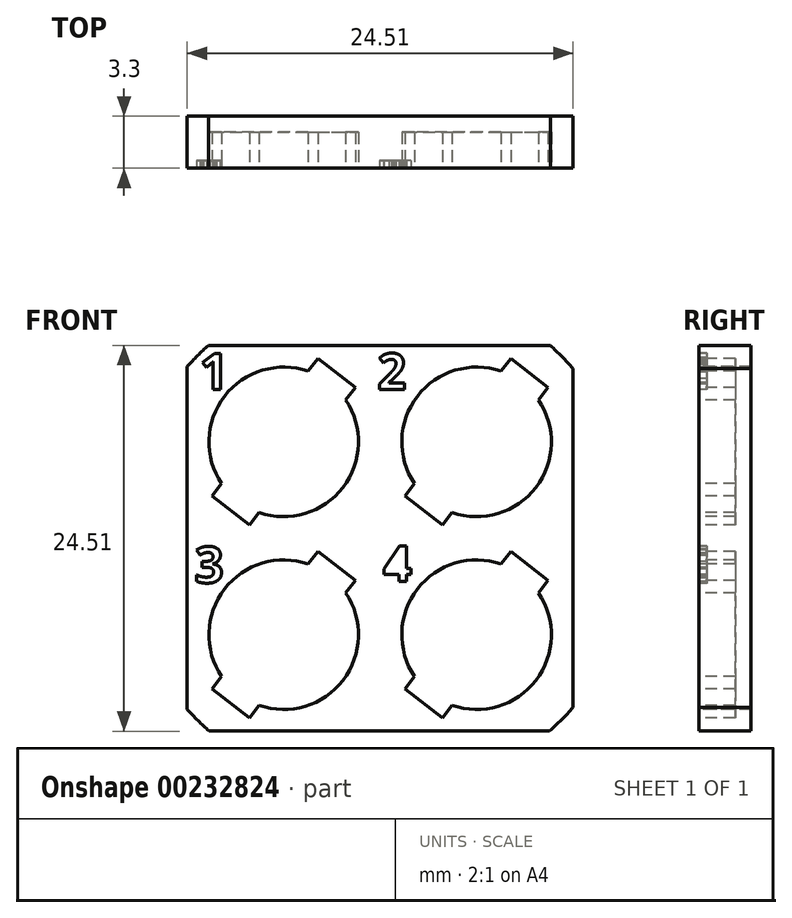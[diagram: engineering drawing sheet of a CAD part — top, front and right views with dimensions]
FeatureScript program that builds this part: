
annotation { "Feature Type Name" : "Feature", "Feature Type Description" : "" }
export const myFeature = defineFeature(function(context is Context, id is Id, definition is map)
    precondition{}
    {
        {
            var Q0;
            Q0=qCreatedBy(makeId("Front.planeOp"),FACE);
            var sketch = newSketch(context, id + "F0", { "sketchPlane" : qUnion([Q0])});
            skLineSegment(sketch, "E0.bottom", {"start": v(6.13, -6.13) * mm, "end": v(-6.12, -6.13) * mm});
            skLineSegment(sketch, "E0.top", {"start": v(6.12, 6.13) * mm, "end": v(-6.13, 6.12) * mm});
            skLineSegment(sketch, "E0.left", {"start": v(6.13, -6.13) * mm, "end": v(6.12, 6.12) * mm});
            skLineSegment(sketch, "E0.right", {"start": v(-6.12, -6.13) * mm, "end": v(-6.13, 6.12) * mm});
            skPoint(sketch, "E0.middle", {"position": v(0, 0) * mm});
            skSolve(sketch);
        }
        {
            var Q0;
            Q0=qSketchRegion(id+"F0",true);
            extrude(context, id + "F1", {"entities" : qUnion([Q0]), "oppositeDirection" : true, "depth" : 3.3 * mm, "offsetDistance" : 25 * mm});
        }
        {
            var Q0;
            Q0=qCreatedBy(makeId("Front.planeOp"),FACE);
            var sketch = newSketch(context, id + "F2", { "sketchPlane" : qUnion([Q0])});
            skCircle(sketch, "E1", {"center": v(0, 0) * mm, "radius": 4.75 * mm});
            skLineSegment(sketch, "E2", {"start": v(1.56, 4.49) * mm, "end": v(2.17, 5.28) * mm});
            skLineSegment(sketch, "E3", {"start": v(2.17, 5.28) * mm, "end": v(4.55, 3.45) * mm});
            skLineSegment(sketch, "E4", {"start": v(4.55, 3.45) * mm, "end": v(3.94, 2.66) * mm});
            skLineSegment(sketch, "E5", {"start": v(-3.94, -2.66) * mm, "end": v(-4.55, -3.45) * mm});
            skLineSegment(sketch, "E6", {"start": v(-4.55, -3.45) * mm, "end": v(-2.17, -5.28) * mm});
            skLineSegment(sketch, "E7", {"start": v(-2.17, -5.28) * mm, "end": v(-1.56, -4.49) * mm});
            skSolve(sketch);
        }
        {
            var Q0;
            {var subQ0=sQuery(id+"F2.wireOp",EDGE,"E5");Q0=makeQuery(id+"F2.imprint","IMPRINT",FACE,{"disambiguationData":[TD([[makeQuery(id+"F2.imprint","IMPRINT",EDGE,{"derivedFrom":subQ0}),1.0]])]});}
            var Q1;
            {var subQ0=sQuery(id+"F2.wireOp",EDGE,"E2");Q1=makeQuery(id+"F2.imprint","IMPRINT",FACE,{"disambiguationData":[TD([[makeQuery(id+"F2.imprint","IMPRINT",EDGE,{"derivedFrom":subQ0}),-1.0]])]});}
            var Q2;
            {var subQ0=sQuery(id+"F2.wireOp",EDGE,"E1");var subQ1=makeQuery(id+"F2.imprint","INTERSECT",VERTEX,{"derivedFrom":[subQ0,sQuery(id+"F2.wireOp",EDGE,"E2")]});Q2=makeQuery(id+"F2.imprint","IMPRINT",FACE,{"disambiguationData":[TD([[makeQuery(id+"F2.imprint","IMPRINT",EDGE,{"disambiguationData":[TD([[subQ1,1.0]])],"derivedFrom":subQ0}),1.0]])]});}
            extrude(context, id + "F3", {"entities" : qUnion([Q0, Q1, Q2]), "operationType" : NewBodyOperationType.REMOVE, "oppositeDirection" : true, "depth" : 2.3 * mm, "offsetDistance" : 25 * mm});
        }
        {
            var Q0;
            Q0=makeQuery(id+"F1.opExtrude","SWEPT_BODY",BODY,{"disambiguationData":[OSD([sQuery(id+"F0.wireOp",EDGE,"E0.bottom"),sQuery(id+"F0.wireOp",EDGE,"E0.top"),sQuery(id+"F0.wireOp",EDGE,"E0.left"),sQuery(id+"F0.wireOp",EDGE,"E0.right")])]});
            transform(context, id + "F4", {"entities" : qUnion([Q0]), "transformType" : TransformType.TRANSLATION_3D, "dx" : -12.25 * mm, "dy" : 0 * mm, "dz" : 0 * mm, "makeCopy" : true});
        }
        {
            var Q0;
            Q0=makeQuery(id+"F1.opExtrude","SWEPT_BODY",BODY,{"disambiguationData":[OSD([sQuery(id+"F0.wireOp",EDGE,"E0.bottom"),sQuery(id+"F0.wireOp",EDGE,"E0.top"),sQuery(id+"F0.wireOp",EDGE,"E0.left"),sQuery(id+"F0.wireOp",EDGE,"E0.right")])]});
            transform(context, id + "F5", {"entities" : qUnion([Q0]), "transformType" : TransformType.TRANSLATION_3D, "dx" : 0 * mm, "dy" : 0 * mm, "dz" : 12.25 * mm, "makeCopy" : true});
        }
        {
            var Q0;
            Q0=makeQuery(id+"F1.opExtrude","SWEPT_BODY",BODY,{"disambiguationData":[OSD([sQuery(id+"F0.wireOp",EDGE,"E0.bottom"),sQuery(id+"F0.wireOp",EDGE,"E0.top"),sQuery(id+"F0.wireOp",EDGE,"E0.left"),sQuery(id+"F0.wireOp",EDGE,"E0.right")])]});
            transform(context, id + "F6", {"entities" : qUnion([Q0]), "transformType" : TransformType.TRANSLATION_3D, "dx" : -12.25 * mm, "dy" : 0 * mm, "dz" : 12.25 * mm, "makeCopy" : true});
        }
        {
            var Q0;
            Q0=makeQuery(id+"F1.opExtrude","SWEPT_BODY",BODY,{"disambiguationData":[OSD([sQuery(id+"F0.wireOp",EDGE,"E0.bottom"),sQuery(id+"F0.wireOp",EDGE,"E0.top"),sQuery(id+"F0.wireOp",EDGE,"E0.left"),sQuery(id+"F0.wireOp",EDGE,"E0.right")])]});
            var Q1;
            Q1=makeQuery(id+"F4.opPattern","COPY",BODY,{"derivedFrom":makeQuery(id+"F1.opExtrude","SWEPT_BODY",BODY,{"disambiguationData":[OSD([sQuery(id+"F0.wireOp",EDGE,"E0.bottom"),sQuery(id+"F0.wireOp",EDGE,"E0.top"),sQuery(id+"F0.wireOp",EDGE,"E0.left"),sQuery(id+"F0.wireOp",EDGE,"E0.right")])]}),"instanceName":"1"});
            var Q2;
            Q2=makeQuery(id+"F5.opPattern","COPY",BODY,{"derivedFrom":makeQuery(id+"F1.opExtrude","SWEPT_BODY",BODY,{"disambiguationData":[OSD([sQuery(id+"F0.wireOp",EDGE,"E0.bottom"),sQuery(id+"F0.wireOp",EDGE,"E0.top"),sQuery(id+"F0.wireOp",EDGE,"E0.left"),sQuery(id+"F0.wireOp",EDGE,"E0.right")])]}),"instanceName":"1"});
            var Q3;
            Q3=makeQuery(id+"F6.opPattern","COPY",BODY,{"derivedFrom":makeQuery(id+"F1.opExtrude","SWEPT_BODY",BODY,{"disambiguationData":[OSD([sQuery(id+"F0.wireOp",EDGE,"E0.bottom"),sQuery(id+"F0.wireOp",EDGE,"E0.top"),sQuery(id+"F0.wireOp",EDGE,"E0.left"),sQuery(id+"F0.wireOp",EDGE,"E0.right")])]}),"instanceName":"1"});
            booleanBodies(context, id + "F7", {"operationType" : BooleanOperationType.UNION, "tools" : qUnion([Q0, Q1, Q2, Q3])});
        }
        {
            var Q0;
            {var subQ0=makeQuery(id+"F1.opExtrude","CAP_FACE",FACE,{"disambiguationData":[OSD([sQuery(id+"F0.wireOp",EDGE,"E0.bottom"),sQuery(id+"F0.wireOp",EDGE,"E0.top"),sQuery(id+"F0.wireOp",EDGE,"E0.left"),sQuery(id+"F0.wireOp",EDGE,"E0.right")])],"isStart":true});Q0=makeQuery(id+"F7.opBoolean","MERGE",FACE,{"derivedFrom":[subQ0,makeQuery(id+"F4.opPattern","COPY",FACE,{"derivedFrom":subQ0,"instanceName":"1"}),makeQuery(id+"F5.opPattern","COPY",FACE,{"derivedFrom":subQ0,"instanceName":"1"}),makeQuery(id+"F6.opPattern","COPY",FACE,{"derivedFrom":subQ0,"instanceName":"1"})]});}
            var sketch = newSketch(context, id + "F8", { "sketchPlane" : qUnion([Q0])});
            skText(sketch, "E8", { "text": "1", "fontName": "OpenSans-Bold.ttf"});
            skPoint(sketch, "E8.secondSnap0", {"position": v(-7.61, 15.58) * mm});
            skText(sketch, "E9", { "text": "2", "fontName": "OpenSans-Bold.ttf"});
            skPoint(sketch, "E9.secondSnap0", {"position": v(-3.98, 15.58) * mm});
            skText(sketch, "E10", { "text": "3", "fontName": "OpenSans-Bold.ttf"});
            skPoint(sketch, "E10.secondSnap0", {"position": v(-16.02, 2.9) * mm});
            skText(sketch, "E11", { "text": "4", "fontName": "OpenSans-Bold.ttf"});
            const initialGuessF8  = {"E8": [-0.01758, 0.01558, 1, 0, 0.0023], "E9": [-0.0063, 0.01558, 1, 0, 0.0023], "E10": [-0.0179, 0.0033, 1, 0, 0.0023], "E11": [-0.00595, 0.00337, 1, 0, 0.0023]};
            skSetInitialGuess(sketch, initialGuessF8);
            skSolve(sketch);
        }
        {
            var Q0;
            Q0=qSketchRegion(id+"F8",true);
            extrude(context, id + "F9", {"entities" : qUnion([Q0]), "operationType" : NewBodyOperationType.REMOVE, "oppositeDirection" : true, "depth" : 0.5 * mm});
        }
        {
            var Q0;
            Q0=qCreatedBy(makeId("Front.planeOp"),FACE);
            var sketch = newSketch(context, id + "F10", { "sketchPlane" : qUnion([Q0])});
            skCircle(sketch, "E12", {"center": v(-6.18, 6.15) * mm, "radius": 16.35 * mm});
            skSolve(sketch);
        }
        {
            var Q0;
            Q0=qSketchRegion(id+"F10",true);
            extrude(context, id + "F11", {"entities" : qUnion([Q0]), "operationType" : NewBodyOperationType.INTERSECT, "oppositeDirection" : true, "depth" : 4.5 * mm, "hasSecondDirection" : true, "secondDirectionOppositeDirection" : false, "secondDirectionDepth" : .5 * mm});
        }
        {
            var Q0;
            Q0=makeQuery(id+"F8.imprint","IMPRINT",FACE,{"disambiguationData":[TD([[makeQuery(id+"F8.imprint","IMPRINT",EDGE,{"derivedFrom":sQuery(id+"F8.wireOp",EDGE,"E11.sketch_text.stroke-11")}),1.0]])]});
            var Q1;
            Q1=makeQuery(id+"F9.opExtrude","CAP_FACE",FACE,{"disambiguationData":[OSD([sQuery(id+"F8.wireOp",EDGE,"E11.sketch_text.stroke-0"),sQuery(id+"F8.wireOp",EDGE,"E11.sketch_text.stroke-1"),sQuery(id+"F8.wireOp",EDGE,"E11.sketch_text.stroke-2"),sQuery(id+"F8.wireOp",EDGE,"E11.sketch_text.stroke-3"),sQuery(id+"F8.wireOp",EDGE,"E11.sketch_text.stroke-4"),sQuery(id+"F8.wireOp",EDGE,"E11.sketch_text.stroke-5"),sQuery(id+"F8.wireOp",EDGE,"E11.sketch_text.stroke-6"),sQuery(id+"F8.wireOp",EDGE,"E11.sketch_text.stroke-7"),sQuery(id+"F8.wireOp",EDGE,"E11.sketch_text.stroke-8"),sQuery(id+"F8.wireOp",EDGE,"E11.sketch_text.stroke-9"),sQuery(id+"F8.wireOp",EDGE,"E11.sketch_text.stroke-10"),sQuery(id+"F8.wireOp",EDGE,"E11.sketch_text.stroke-11"),sQuery(id+"F8.wireOp",EDGE,"E11.sketch_text.stroke-12"),sQuery(id+"F8.wireOp",EDGE,"E11.sketch_text.stroke-13"),sQuery(id+"F8.wireOp",EDGE,"E11.sketch_text.stroke-14"),sQuery(id+"F8.wireOp",EDGE,"E11.sketch_text.stroke-15"),sQuery(id+"F8.wireOp",EDGE,"E11.sketch_text.stroke-16"),sQuery(id+"F8.wireOp",EDGE,"E11.sketch_text.stroke-17")])],"isStart":false});
            extrude(context, id + "F12", {"entities" : qUnion([Q0]), "operationType" : NewBodyOperationType.REMOVE, "oppositeDirection" : true, "endBoundEntityFace" : qUnion([Q1]), "depth" : 0.5 * mm});
        }
    });
